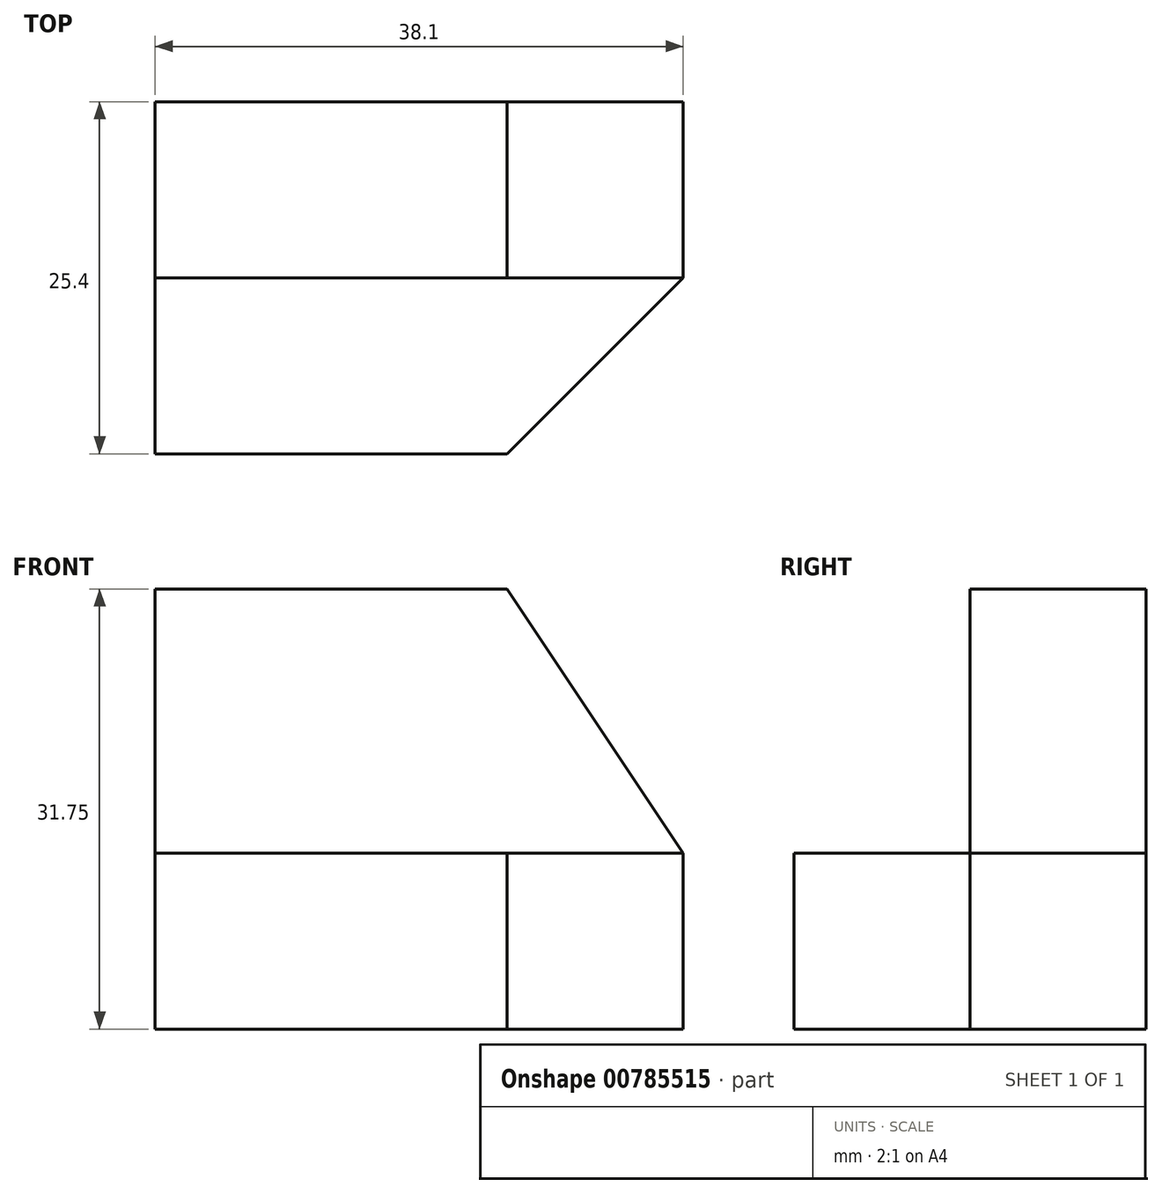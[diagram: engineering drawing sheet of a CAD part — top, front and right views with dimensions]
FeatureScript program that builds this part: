
annotation { "Feature Type Name" : "Feature", "Feature Type Description" : "" }
export const myFeature = defineFeature(function(context is Context, id is Id, definition is map)
    precondition{}
    {
        {
            var Q0;
            Q0=qCreatedBy(makeId("Front.planeOp"),FACE);
            var sketch = newSketch(context, id + "F0", { "sketchPlane" : qUnion([Q0])});
            skLineSegment(sketch, "E0", {"start": v(0, 0) * mm, "end": v(-38.1, 0) * mm});
            skLineSegment(sketch, "E1", {"start": v(-38.1, 0) * mm, "end": v(-38.1, 31.75) * mm});
            skLineSegment(sketch, "E2", {"start": v(-38.1, 31.75) * mm, "end": v(-12.7, 31.75) * mm});
            skLineSegment(sketch, "E3", {"start": v(0, 0) * mm, "end": v(0, 12.7) * mm});
            skLineSegment(sketch, "E4", {"start": v(0, 12.7) * mm, "end": v(-12.7, 31.75) * mm});
            skSolve(sketch);
        }
        {
            var Q0;
            Q0 = qSketchRegion(id + "F0", true);
            extrude(context, id + "F1", {"entities" : qUnion([Q0]), "depth" : 12.7 * mm, "offsetDistance" : 25.4 * mm});
        }
        {
            var Q0;
            Q0=makeQuery(id+"F1.opExtrude","CAP_FACE",FACE,{"disambiguationData":[OSD([sQuery(id+"F0.wireOp",EDGE,"E0"),sQuery(id+"F0.wireOp",EDGE,"E1"),sQuery(id+"F0.wireOp",EDGE,"E2"),sQuery(id+"F0.wireOp",EDGE,"E3"),sQuery(id+"F0.wireOp",EDGE,"E4")])],"isStart":false});
            var sketch = newSketch(context, id + "F2", { "sketchPlane" : qUnion([Q0])});
            skLineSegment(sketch, "E5", {"start": v(-38.1, 0) * mm, "end": v(-38.1, 12.7) * mm});
            skLineSegment(sketch, "E6", {"start": v(-38.1, 12.7) * mm, "end": v(0, 12.7) * mm});
            skLineSegment(sketch, "E7", {"start": v(0, 12.7) * mm, "end": v(0, 0) * mm});
            skLineSegment(sketch, "E8", {"start": v(0, 0) * mm, "end": v(-38.1, 0) * mm});
            skSolve(sketch);
        }
        {
            var Q0;
            Q0=makeQuery(id+"F2.imprint","IMPRINT",FACE,{"disambiguationData":[TD([[makeQuery(id+"F2.imprint","IMPRINT",EDGE,{"derivedFrom":sQuery(id+"F2.wireOp",EDGE,"E5")}),-1.0]])]});
            extrude(context, id + "F3", {"entities" : qUnion([Q0]), "operationType" : NewBodyOperationType.ADD, "depth" : 12.7 * mm, "offsetDistance" : 25.4 * mm});
        }
        {
            var Q0;
            Q0=makeQuery(id+"F3.opExtrude","SWEPT_FACE",FACE,{"disambiguationData":[OSD([sQuery(id+"F2.wireOp",EDGE,"E6")])]});
            var sketch = newSketch(context, id + "F4", { "sketchPlane" : qUnion([Q0])});
            skLineSegment(sketch, "E9", {"start": v(0, -25.4) * mm, "end": v(-12.7, -25.4) * mm});
            skLineSegment(sketch, "E10", {"start": v(-12.7, -25.4) * mm, "end": v(0, -12.7) * mm});
            skLineSegment(sketch, "E11", {"start": v(0, -12.7) * mm, "end": v(0, -25.4) * mm});
            skSolve(sketch);
        }
        {
            var Q0;
            Q0=makeQuery(id+"F4.imprint","IMPRINT",FACE,{"disambiguationData":[TD([[makeQuery(id+"F4.imprint","IMPRINT",EDGE,{"derivedFrom":sQuery(id+"F4.wireOp",EDGE,"E9")}),1.0]])]});
            var sketch = newSketch(context, id + "F5", { "sketchPlane" : qUnion([Q0])});
            skSolve(sketch);
        }
        {
            var Q0;
            Q0 = qSketchRegion(id + "F5", true);
            var Q1;
            Q1=makeQuery(id+"F4.imprint","IMPRINT",FACE,{"disambiguationData":[TD([[makeQuery(id+"F4.imprint","IMPRINT",EDGE,{"derivedFrom":sQuery(id+"F4.wireOp",EDGE,"E9")}),1.0]])]});
            extrude(context, id + "F6", {"entities" : qUnion([Q0, Q1]), "operationType" : NewBodyOperationType.REMOVE, "oppositeDirection" : true, "depth" : 12.7 * mm, "offsetDistance" : 25.4 * mm});
        }
    });
